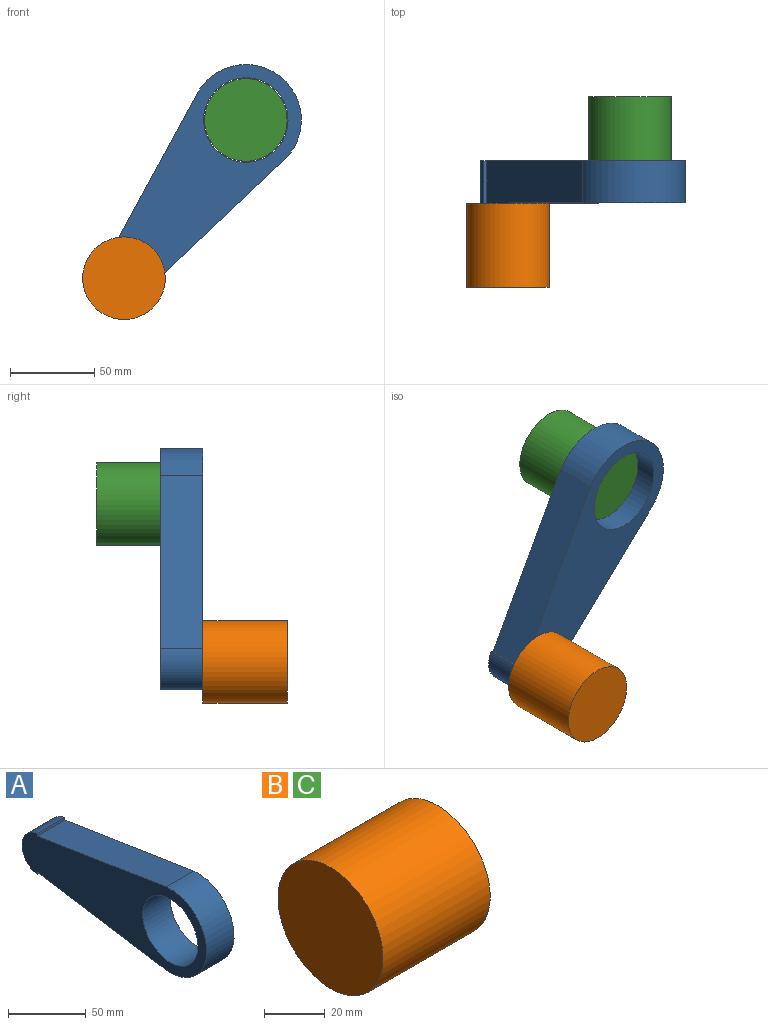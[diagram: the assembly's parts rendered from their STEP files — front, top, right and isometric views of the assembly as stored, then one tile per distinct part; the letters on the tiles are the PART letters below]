
ASSEMBLY  parts=3 mates=2
PART A: 117 faces, bbox 25x167.8x65.9 mm
  f0: plane 167.78x65.89mm, normal (1,0,0), area 5512.4mm2, adj f1,f2,f3,f5,f6,f7,f8,f9
  f1: plane 113.07x25mm, normal (0,0.16,-0.99), area 2861.8mm2, adj f0,f3,f4,f114
  f2: plane 117.09x25mm, normal (0,0.16,0.99), area 2963.7mm2, adj f0,f3,f4,f115
  f3: cylinder r=32.94mm len=65.89mm, axis (-1,0,0), area 2870.8mm2, adj f0,f1,f2,f4
  f4: plane 167.78x65.89mm, normal (-1,0,0), area 5810.4mm2, adj f1,f2,f3,f5,f114,f115,f116
  f5: cylinder r=25.06mm len=50.11mm, axis (1,0,0), area 3935.6mm2, adj f0,f4
  f6: extruded ~10x2.09mm, area 22.9mm2, adj f0,f7,f30,f31
  f7: extruded ~10x3.03mm, area 34.8mm2, adj f0,f6,f8,f31
  f8: extruded ~10x2.21mm, area 24mm2, adj f0,f7,f9,f31
  f9: extruded ~10x0.83mm, area 10.8mm2, adj f0,f8,f10,f31
  f10: extruded ~10x0.86mm, area 9.2mm2, adj f0,f9,f11,f31
  f11: extruded ~10x1.17mm, area 14.3mm2, adj f0,f10,f12,f31
  f12: extruded ~10x2.05mm, area 21.2mm2, adj f0,f11,f13,f31
  f13: extruded ~10x3.44mm, area 35.5mm2, adj f0,f12,f14,f31
  f14: plane 10x1.56mm, normal (0,-0.92,0.4), area 17mm2, adj f0,f13,f15,f31
  f15: extruded ~10x3.99mm, area 41mm2, adj f0,f14,f16,f31
  f16: extruded ~10x3.44mm, area 36.1mm2, adj f0,f15,f17,f31
  f17: extruded ~10x2.44mm, area 28.6mm2, adj f0,f16,f18,f31
  f18: extruded ~10x1.48mm, area 15.5mm2, adj f0,f17,f19,f31
  f19: extruded ~10x1.11mm, area 15.8mm2, adj f0,f18,f20,f31
  f20: extruded ~10x2.5mm, area 27.6mm2, adj f0,f19,f21,f31
  f21: extruded ~10x2.49mm, area 27.9mm2, adj f0,f20,f22,f31
  f22: extruded ~10x1.26mm, area 14.6mm2, adj f0,f21,f23,f31
  f23: extruded ~10x1.46mm, area 17.5mm2, adj f0,f22,f24,f31
  f24: extruded ~10x2.3mm, area 23.8mm2, adj f0,f23,f25,f31
  f25: extruded ~10x2.01mm, area 20.3mm2, adj f0,f24,f26,f31
  f26: extruded ~10x1.95mm, area 20.9mm2, adj f0,f25,f27,f31
  f27: plane 10x1.77mm, normal (0,1,0), area 17.7mm2, adj f0,f26,f28,f31
  f28: extruded ~10x3.91mm, area 40.4mm2, adj f0,f27,f29,f31
  f29: extruded ~10x3.69mm, area 38.7mm2, adj f0,f28,f30,f31
  f30: extruded ~10x2.72mm, area 31.4mm2, adj f0,f6,f29,f31
  f31: plane 13.08x8.95mm, normal (1,0,0), area 48.9mm2, adj f6,f7,f8,f9,f10,f11,f12,f13
  f32: extruded ~10x1.49mm, area 16.6mm2, adj f0,f33,f50,f51
  f33: extruded ~10x1.75mm, area 18.7mm2, adj f0,f32,f34,f51
  f34: plane 10x7.43mm, normal (0,-1,0), area 74.3mm2, adj f0,f33,f35,f51
  f35: plane 10x3.66mm, normal (0,0,1), area 36.6mm2, adj f0,f34,f36,f51
  f36: plane 10x1.49mm, normal (0,-1,0), area 14.8mm2, adj f0,f35,f37,f51
  f37: plane 10x3.66mm, normal (0,0,-1), area 36.6mm2, adj f0,f36,f38,f51
  f38: plane 10x2.93mm, normal (0,-1,0), area 29.3mm2, adj f0,f37,f39,f51
  f39: plane 10x1.11mm, normal (0,0,-1), area 11.1mm2, adj f0,f38,f40,f51
  f40: plane 10x2.69mm, normal (0,0.96,-0.29), area 28.1mm2, adj f0,f39,f41,f51
  f41: plane 10x1.81mm, normal (0,0.4,-0.92), area 19.8mm2, adj f0,f40,f42,f51
  f42: plane 10x0.92mm, normal (0,1,0), area 9.2mm2, adj f0,f41,f43,f51
  f43: plane 10x1.81mm, normal (0,0,1), area 18.1mm2, adj f0,f42,f44,f51
  f44: plane 10x7.51mm, normal (0,1,0), area 75.1mm2, adj f0,f43,f45,f51
  f45: extruded ~10x3.86mm, area 61mm2, adj f0,f44,f46,f51
  f46: extruded ~10x1.09mm, area 11mm2, adj f0,f45,f47,f51
  f47: extruded ~10x0.91mm, area 9.5mm2, adj f0,f46,f48,f51
  f48: plane 10x1.46mm, normal (0,-1,0), area 14.6mm2, adj f0,f47,f49,f51
  f49: extruded ~10x0.75mm, area 7.6mm2, adj f0,f48,f50,f51
  f50: extruded ~10x0.98mm, area 9.8mm2, adj f0,f32,f49,f51
  f51: plane 15.78x7.47mm, normal (1,0,0), area 41.2mm2, adj f32,f33,f34,f35,f36,f37,f38,f39
  f52: extruded ~10x2.18mm, area 21.9mm2, adj f0,f53,f70,f71
  f53: extruded ~10x1.92mm, area 20.2mm2, adj f0,f52,f54,f71
  f54: plane 10x1.71mm, normal (0,-1,0), area 17.1mm2, adj f0,f53,f55,f71
  f55: extruded ~10x4.03mm, area 41.5mm2, adj f0,f54,f56,f71
  f56: extruded ~10x3mm, area 33.1mm2, adj f0,f55,f57,f71
  f57: extruded ~10x3.37mm, area 36.3mm2, adj f0,f56,f58,f71
  f58: plane 10x8.69mm, normal (0,0,1), area 86.9mm2, adj f0,f57,f59,f71
  f59: plane 10x1.21mm, normal (0,-1,0), area 12.1mm2, adj f0,f58,f60,f71
  f60: extruded ~10x4.12mm, area 44.4mm2, adj f0,f59,f61,f71
  f61: extruded ~10x3.75mm, area 42mm2, adj f0,f60,f62,f71
  f62: extruded ~10x4.04mm, area 45.8mm2, adj f0,f61,f63,f71
  f63: extruded ~10x4.85mm, area 51.9mm2, adj f0,f62,f64,f71
  f64: extruded ~10x4.73mm, area 51.3mm2, adj f0,f63,f70,f71
  f65: extruded ~10x2.31mm, area 25.8mm2, adj f66,f69,f71,f72
  f66: extruded ~10x2.77mm, area 29.4mm2, adj f65,f67,f71,f72
  f67: plane 10x6.6mm, normal (0,0,-1), area 66mm2, adj f66,f68,f71,f72
  f68: extruded ~10x2.74mm, area 29.9mm2, adj f67,f69,f71,f72
  f69: extruded ~10x2.42mm, area 27mm2, adj f65,f68,f71,f72
  f70: extruded ~10x4.42mm, area 48.7mm2, adj f0,f52,f64,f71
  f71: plane 13.08x10.68mm, normal (1,0,0), area 63.5mm2, adj f52,f53,f54,f55,f56,f57,f58,f59
  f72: plane 6.6x3.73mm, normal (1,0,0), area 19.8mm2, adj f65,f66,f67,f68,f69
  f73: extruded ~10x2.18mm, area 21.9mm2, adj f0,f74,f91,f92
  f74: extruded ~10x1.92mm, area 20.2mm2, adj f0,f73,f75,f92
  f75: plane 10x1.71mm, normal (0,-1,0), area 17.1mm2, adj f0,f74,f76,f92
  f76: extruded ~10x4.03mm, area 41.5mm2, adj f0,f75,f77,f92
  f77: extruded ~10x3mm, area 33.1mm2, adj f0,f76,f78,f92
  f78: extruded ~10x3.37mm, area 36.3mm2, adj f0,f77,f79,f92
  f79: plane 10x8.69mm, normal (0,0,1), area 86.9mm2, adj f0,f78,f80,f92
  f80: plane 10x1.21mm, normal (0,-1,0), area 12.1mm2, adj f0,f79,f81,f92
  f81: extruded ~10x4.12mm, area 44.4mm2, adj f0,f80,f82,f92
  f82: extruded ~10x3.75mm, area 42mm2, adj f0,f81,f83,f92
  f83: extruded ~10x4.04mm, area 45.8mm2, adj f0,f82,f84,f92
  f84: extruded ~10x4.85mm, area 51.9mm2, adj f0,f83,f85,f92
  f85: extruded ~10x4.73mm, area 51.3mm2, adj f0,f84,f91,f92
  f86: extruded ~10x2.31mm, area 25.8mm2, adj f87,f90,f92,f93
  f87: extruded ~10x2.77mm, area 29.4mm2, adj f86,f88,f92,f93
  f88: plane 10x6.6mm, normal (0,0,-1), area 66mm2, adj f87,f89,f92,f93
  f89: extruded ~10x2.74mm, area 29.9mm2, adj f88,f90,f92,f93
  f90: extruded ~10x2.42mm, area 27mm2, adj f86,f89,f92,f93
  f91: extruded ~10x4.42mm, area 48.7mm2, adj f0,f73,f85,f92
  f92: plane 13.08x10.68mm, normal (1,0,0), area 63.5mm2, adj f73,f74,f75,f76,f77,f78,f79,f80
  f93: plane 6.6x3.73mm, normal (1,0,0), area 19.8mm2, adj f86,f87,f88,f89,f90
  f94: extruded ~10x1.49mm, area 16.6mm2, adj f0,f95,f112,f113
  f95: extruded ~10x1.75mm, area 18.7mm2, adj f0,f94,f96,f113
  f96: plane 10x7.43mm, normal (0,-1,0), area 74.3mm2, adj f0,f95,f97,f113
  f97: plane 10x3.66mm, normal (0,0,1), area 36.6mm2, adj f0,f96,f98,f113
  f98: plane 10x1.49mm, normal (0,-1,0), area 14.8mm2, adj f0,f97,f99,f113
  f99: plane 10x3.66mm, normal (0,0,-1), area 36.6mm2, adj f0,f98,f100,f113
  f100: plane 10x2.93mm, normal (0,-1,0), area 29.3mm2, adj f0,f99,f101,f113
  f101: plane 10x1.11mm, normal (0,0,-1), area 11.1mm2, adj f0,f100,f102,f113
  f102: plane 10x2.69mm, normal (0,0.96,-0.29), area 28.1mm2, adj f0,f101,f103,f113
  f103: plane 10x1.81mm, normal (0,0.4,-0.92), area 19.8mm2, adj f0,f102,f104,f113
  f104: plane 10x0.92mm, normal (0,1,0), area 9.2mm2, adj f0,f103,f105,f113
  f105: plane 10x1.81mm, normal (0,0,1), area 18.1mm2, adj f0,f104,f106,f113
  f106: plane 10x7.51mm, normal (0,1,0), area 75.1mm2, adj f0,f105,f107,f113
  f107: extruded ~10x3.86mm, area 61mm2, adj f0,f106,f108,f113
  f108: extruded ~10x1.09mm, area 11mm2, adj f0,f107,f109,f113
  f109: extruded ~10x0.91mm, area 9.5mm2, adj f0,f108,f110,f113
  f110: plane 10x1.46mm, normal (0,-1,0), area 14.6mm2, adj f0,f109,f111,f113
  f111: extruded ~10x0.75mm, area 7.6mm2, adj f0,f110,f112,f113
  f112: extruded ~10x0.98mm, area 9.8mm2, adj f0,f94,f111,f113
  f113: plane 15.78x7.47mm, normal (1,0,0), area 41.2mm2, adj f94,f95,f96,f97,f98,f99,f100,f101
  f114: plane 25x1.98mm, normal (0,-0.99,-0.16), area 50mm2, adj f0,f1,f4,f116
  f115: plane 25x1.98mm, normal (0,-0.99,0.16), area 50mm2, adj f0,f2,f4,f116
  f116: cylinder r=16.37mm len=32.34mm, axis (-1,0,0), area 1157.5mm2, adj f0,f4,f114,f115
PART B: 3 faces, bbox 50x49x49 mm
  f0: cylinder r=24.5mm len=50mm, axis (-1,0,0), area 7696.9mm2, adj f1,f2
  f1: plane 49x49mm, normal (1,0,0), area 1885.7mm2, adj f0
  f2: plane 49x49mm, normal (-1,0,0), area 1885.7mm2, adj f0
PART C: same geometry as B
PLACE A rot(axis=(-0.4,-0.4,0.82),101.2deg) t=(-42.92,-13,-55.7)mm
PLACE B rot(axis=(0.67,0.67,0.33),143.6deg) t=(-72.31,-63,-93.84)mm
PLACE C rot(axis=(0.58,-0.58,-0.58),120deg) t=(0,50,0)mm
MATE revolute A.f3 <-> C.f0  axis (0,1,0) through (0,12,0)mm
MATE fastened B.f0 <-> A.f116  axis (0,1,0) through (-72.31,-13,-93.84)mm
